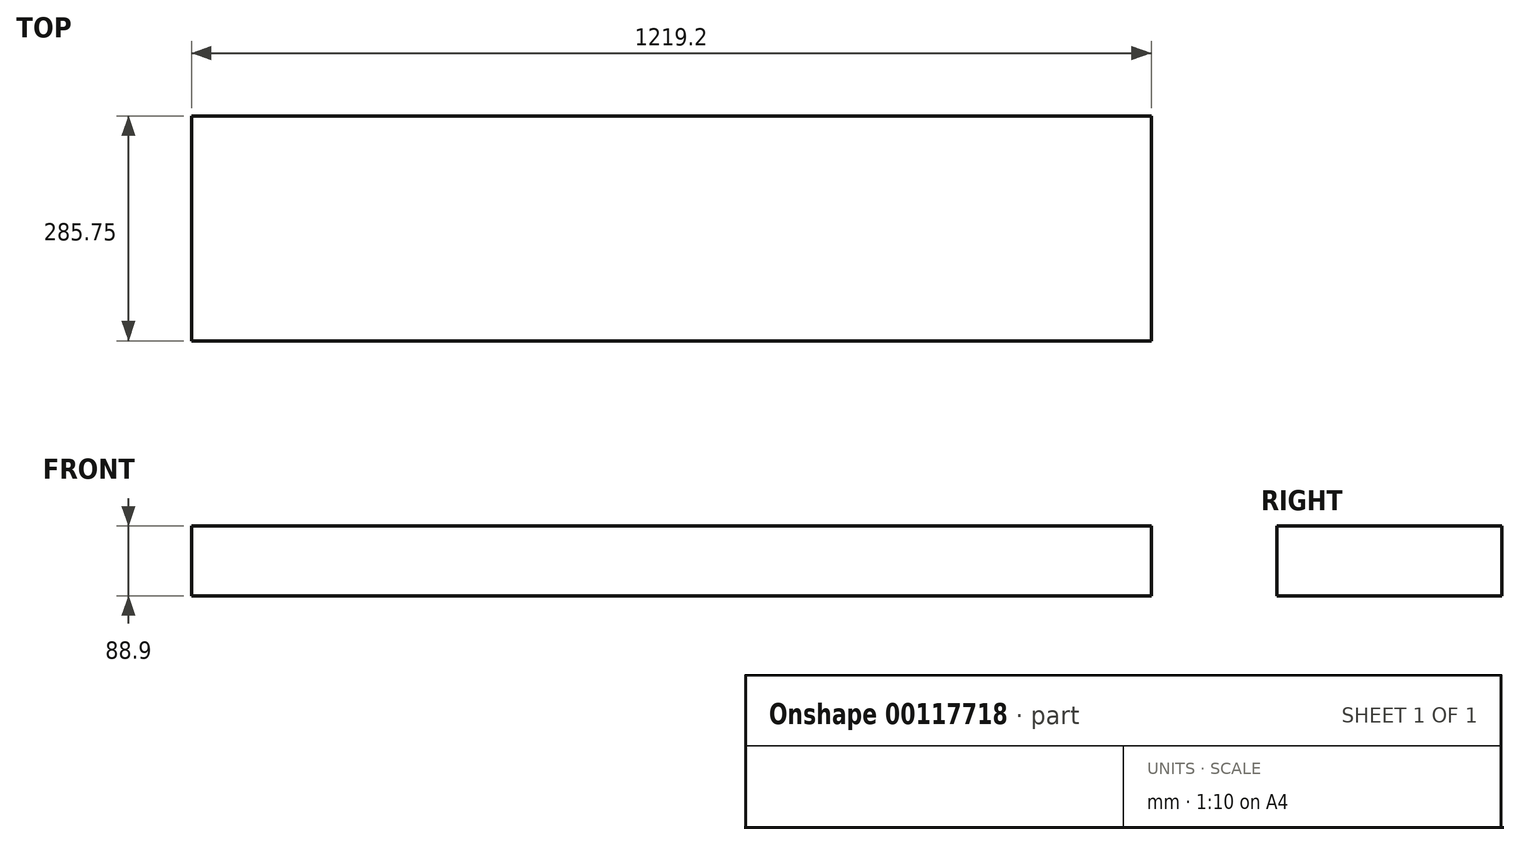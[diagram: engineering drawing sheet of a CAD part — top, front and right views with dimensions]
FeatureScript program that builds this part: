
annotation { "Feature Type Name" : "Feature", "Feature Type Description" : "" }
export const myFeature = defineFeature(function(context is Context, id is Id, definition is map)
    precondition{}
    {
        {
            var Q0;
            Q0=qCreatedBy(makeId("Top.planeOp"),FACE);
            var sketch = newSketch(context, id + "F0", { "sketchPlane" : qUnion([Q0])});
            skLineSegment(sketch, "E0.bottom", {"start": v(-610.09, 156.61) * mm, "end": v(609.11, 156.61) * mm});
            skLineSegment(sketch, "E0.top", {"start": v(-610.09, -129.14) * mm, "end": v(609.11, -129.14) * mm});
            skLineSegment(sketch, "E0.left", {"start": v(-610.09, 156.61) * mm, "end": v(-610.09, -129.14) * mm});
            skLineSegment(sketch, "E0.right", {"start": v(609.11, 156.61) * mm, "end": v(609.11, -129.14) * mm});
            skSolve(sketch);
        }
        {
            var Q0;
            Q0 = qSketchRegion(id + "F0", true);
            extrude(context, id + "F1", {"entities" : qUnion([Q0]), "depth" : 88.9 * mm});
        }
    });
